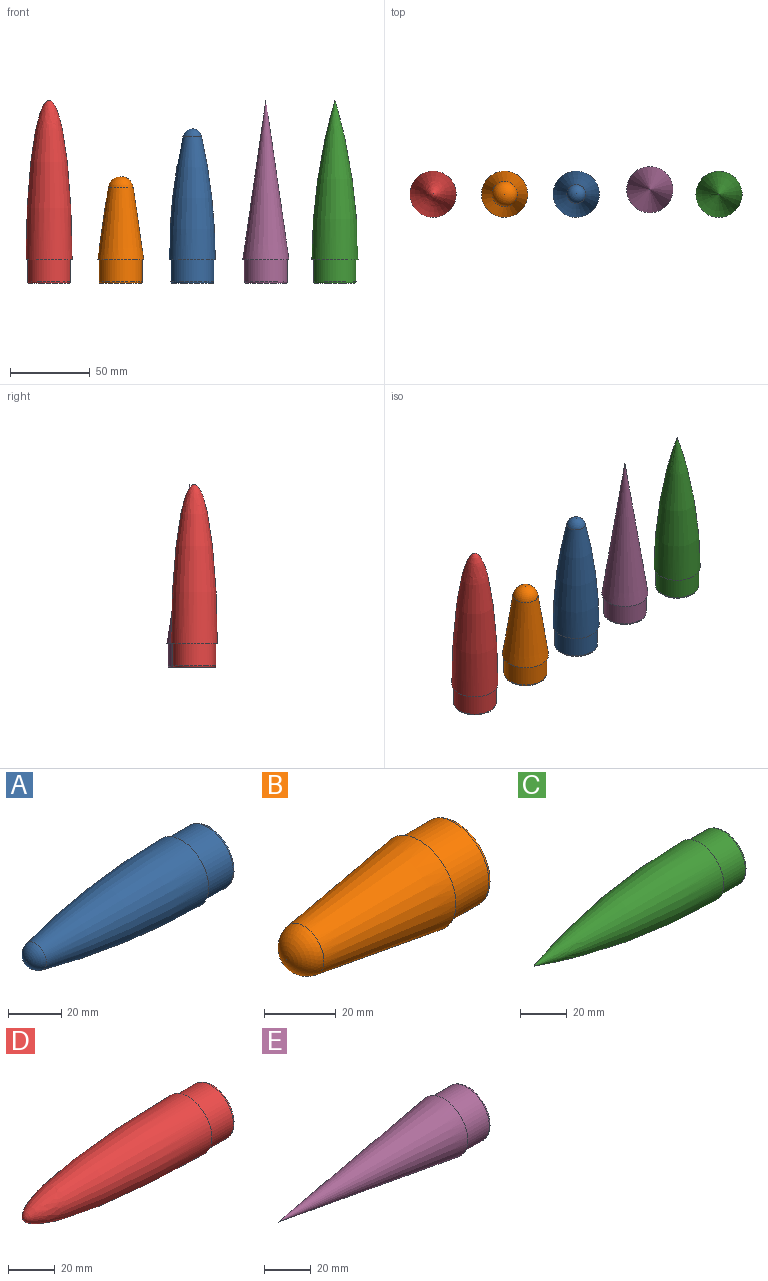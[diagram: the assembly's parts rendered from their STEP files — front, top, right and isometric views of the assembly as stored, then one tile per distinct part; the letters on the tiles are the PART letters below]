
ASSEMBLY  parts=5 mates=4
PART A: 6 faces, bbox 97.2x29.2x29.2 mm
  f0: revolved ~77.55x29mm, area 5705.4mm2, adj f1,f5
  f1: sphere r=6mm, area 176.4mm2, adj f0
  f2: plane 25x25mm, normal (1,0,0), area 490.9mm2, adj f3
  f3: torus R=12.5mm, axis (-1,0,0), area 129.7mm2, adj f2,f4
  f4: cylinder r=13.5mm len=27mm, axis (-1,0,0), area 1187.5mm2, adj f3,f5
  f5: plane 29x29mm, normal (1,0,0), area 88mm2, adj f0,f4
PART B: 6 faces, bbox 67.3x29.2x29.2 mm
  f0: cone r=7.92mm half-angle=8.3deg, axis (1,0,0), area 3230.7mm2, adj f1,f5
  f1: sphere r=8mm, area 344.4mm2, adj f0
  f2: plane 25x25mm, normal (1,0,0), area 490.9mm2, adj f3
  f3: torus R=12.5mm, axis (-1,0,0), area 129.7mm2, adj f2,f4
  f4: cylinder r=13.5mm len=27mm, axis (-1,0,0), area 1187.5mm2, adj f3,f5
  f5: plane 29x29mm, normal (1,0,0), area 88mm2, adj f0,f4
PART C: 5 faces, bbox 115x29.2x29.2 mm
  f0: plane 29x29mm, normal (1,0,0), area 88mm2, adj f1,f4
  f1: revolved ~100x29mm, area 6150mm2, adj f0
  f2: plane 25x25mm, normal (1,0,0), area 490.9mm2, adj f3
  f3: torus R=12.5mm, axis (1,0,0), area 129.7mm2, adj f2,f4
  f4: cylinder r=13.5mm len=27mm, axis (1,0,0), area 1187.5mm2, adj f0,f3
PART D: 5 faces, bbox 73x87.2x87.2 mm
  f0: plane 87x87mm, normal (1,0,0), area 88mm2, adj f1,f4
  f1: revolved ~29x14.5mm, area 0mm2, adj f0
  f2: plane 25x25mm, normal (1,0,0), area 490.9mm2, adj f3
  f3: torus R=12.5mm, axis (1,0,0), area 129.7mm2, adj f2,f4
  f4: cylinder r=13.5mm len=27mm, axis (1,0,0), area 1187.5mm2, adj f0,f3
PART E: 5 faces, bbox 115x29.2x29.2 mm
  f0: cylinder r=13.5mm len=27mm, axis (-1,0,0), area 1187.5mm2, adj f1,f4
  f1: plane 29x29mm, normal (1,0,0), area 88mm2, adj f0,f2
  f2: cone r=0mm half-angle=8.3deg, axis (1,0,0), area 4602.9mm2, adj f1
  f3: plane 25x25mm, normal (1,0,0), area 490.9mm2, adj f4
  f4: torus R=12.5mm, axis (-1,0,0), area 129.7mm2, adj f0,f3
PLACE A rot(axis=(0,1,0),90deg) t=(90,0,100)mm
PLACE B rot(axis=(0,1,0),90deg) t=(45,0,100)mm
PLACE C rot(axis=(0,1,0),90deg) t=(179.78,-0.09,100)mm
PLACE D rot(axis=(0,1,0),90deg) t=(0,0,100)mm
PLACE E rot(axis=(0,1,0),90deg) t=(136.33,2.88,100)mm
MATE planar B.f0 <-> D.f3  axis (0,0,-1) through (45,0,0)mm
MATE planar D.f3 <-> A.f3  axis (0,0,-1) through (0,0,0)mm
MATE planar D.f3 <-> C.f3  axis (0,0,-1) through (0,0,0)mm
MATE planar E.f0 <-> A.f3  axis (0,0,-1) through (136.33,2.88,0)mm
